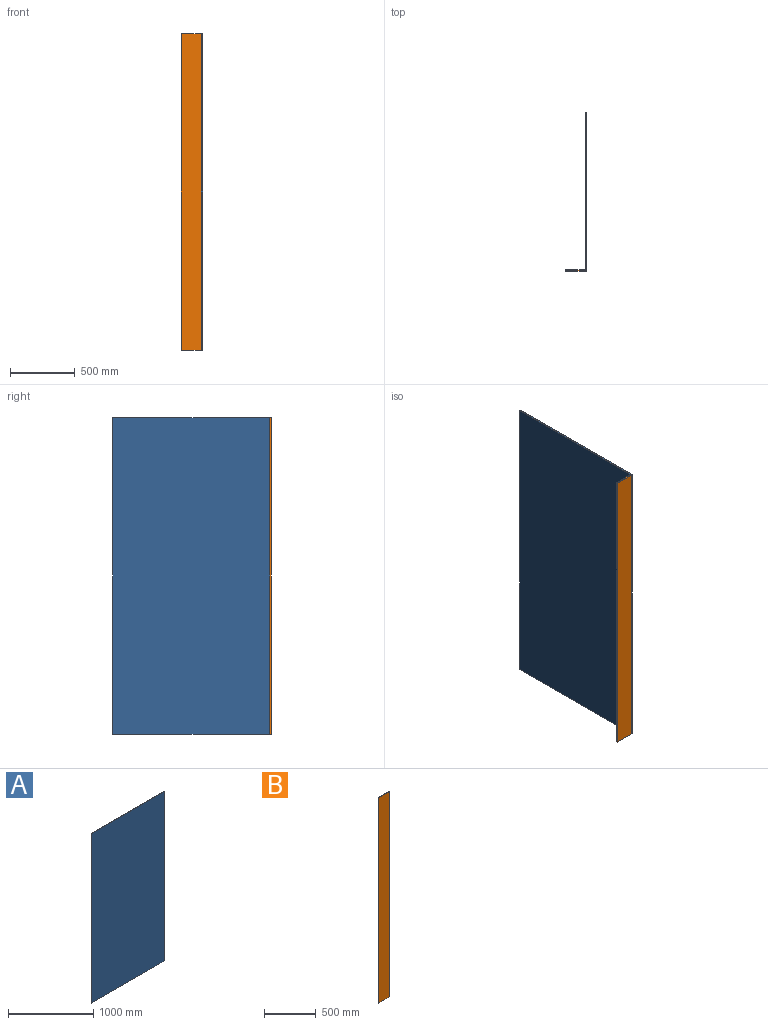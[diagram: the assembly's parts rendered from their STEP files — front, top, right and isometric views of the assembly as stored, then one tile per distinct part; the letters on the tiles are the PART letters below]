
ASSEMBLY  parts=2 mates=1
PART A: 6 faces, bbox 1219.2x9.9x2438.4 mm
  f0: plane 2438.4x9.92mm, normal (1,0,0), area 24193.5mm2, adj f1,f3,f4,f5
  f1: plane 1219.2x9.92mm, normal (0,0,1), area 12096.8mm2, adj f0,f2,f4,f5
  f2: plane 2438.4x9.92mm, normal (-1,0,0), area 24193.5mm2, adj f1,f3,f4,f5
  f3: plane 1219.2x9.92mm, normal (0,0,-1), area 12096.8mm2, adj f0,f2,f4,f5
  f4: plane 2438.4x1219.2mm, normal (0,-1,0), area 2972897.3mm2, adj f0,f1,f2,f3
  f5: plane 2438.4x1219.2mm, normal (0,1,0), area 2972897.3mm2, adj f0,f1,f2,f3
PART B: 6 faces, bbox 152.4x9.9x2438.4 mm
  f0: plane 2438.4x9.92mm, normal (1,0,0), area 24193.5mm2, adj f1,f3,f4,f5
  f1: plane 152.4x9.92mm, normal (0,0,1), area 1512.1mm2, adj f0,f2,f4,f5
  f2: plane 2438.4x9.92mm, normal (-1,0,0), area 24193.5mm2, adj f1,f3,f4,f5
  f3: plane 152.4x9.92mm, normal (0,0,-1), area 1512.1mm2, adj f0,f2,f4,f5
  f4: plane 2438.4x152.4mm, normal (0,-1,0), area 371612.2mm2, adj f0,f1,f2,f3
  f5: plane 2438.4x152.4mm, normal (0,1,0), area 371612.2mm2, adj f0,f1,f2,f3
PLACE A rot(axis=(0.71,-0.71,0),180deg) t=(-1520.11,-524,2922.4)mm
PLACE B rot(axis=(1,0,0),180deg) t=(-1601.27,-1128.64,2922.4)mm
MATE planar B.f0 <-> A.f5  axis (1,0,0) through (-1525.07,-1133.6,1703.2)mm
